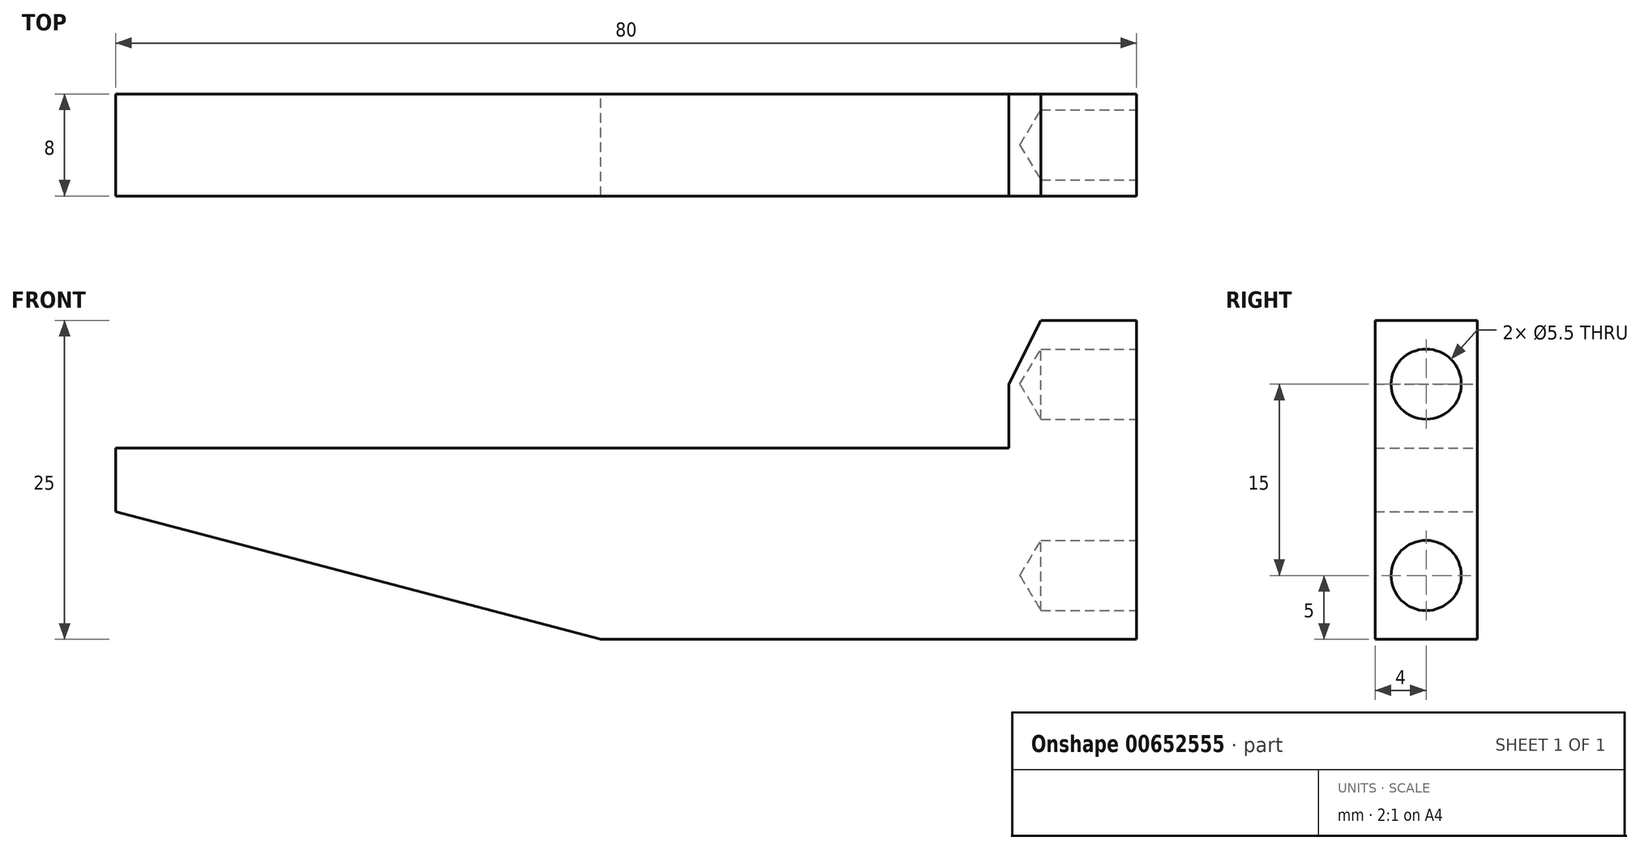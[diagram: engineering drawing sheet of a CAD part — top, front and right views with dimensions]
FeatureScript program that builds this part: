
annotation { "Feature Type Name" : "Feature", "Feature Type Description" : "" }
export const myFeature = defineFeature(function(context is Context, id is Id, definition is map)
    precondition{}
    {
        {
            var Q0;
            Q0=qCreatedBy(makeId("Front.planeOp"),FACE);
            var sketch = newSketch(context, id + "F0", { "sketchPlane" : qUnion([Q0])});
            skLineSegment(sketch, "E0", {"start": v(0, 0) * mm, "end": v(42, 0) * mm});
            skLineSegment(sketch, "E1", {"start": v(42, 0) * mm, "end": v(42, 25) * mm});
            skLineSegment(sketch, "E2", {"start": v(42, 25) * mm, "end": v(34.5, 25) * mm});
            skLineSegment(sketch, "E3", {"start": v(34.5, 25) * mm, "end": v(32, 20) * mm});
            skLineSegment(sketch, "E4", {"start": v(32, 20) * mm, "end": v(32, 15) * mm});
            skLineSegment(sketch, "E5", {"start": v(32, 15) * mm, "end": v(-38, 15) * mm});
            skLineSegment(sketch, "E6", {"start": v(-38, 15) * mm, "end": v(-38, 10) * mm});
            skLineSegment(sketch, "E7", {"start": v(-38, 10) * mm, "end": v(0, 0) * mm});
            skSolve(sketch);
        }
        {
            var Q0;
            Q0=makeQuery(id+"F0.imprint","IMPRINT",FACE,{"disambiguationData":[TD([[makeQuery(id+"F0.imprint","IMPRINT",EDGE,{"derivedFrom":sQuery(id+"F0.wireOp",EDGE,"E0")}),1.0]])]});
            extrude(context, id + "F1", {"entities" : qUnion([Q0]), "depth" : 4 * mm, "offsetDistance" : 25 * mm, "hasSecondDirection" : true, "secondDirectionOppositeDirection" : true, "secondDirectionDepth" : 4 * mm});
        }
        {
            var Q0;
            Q0=makeQuery(id+"F1.opExtrude","SWEPT_FACE",FACE,{"disambiguationData":[OSD([sQuery(id+"F0.wireOp",EDGE,"E1")])]});
            var sketch = newSketch(context, id + "F2", { "sketchPlane" : qUnion([Q0])});
            skPoint(sketch, "E8", {"position": v(0, 20) * mm});
            skPoint(sketch, "E9", {"position": v(0, 5) * mm});
            skSolve(sketch);
        }
        {
            var Q0;
            Q0=sQuery(id+"F2.wireOp",VERTEX,"E8");
            var Q1;
            Q1=sQuery(id+"F2.wireOp",VERTEX,"E9");
            var Q2;
            Q2=makeQuery(id+"F1.opExtrude","SWEPT_BODY",BODY,{"disambiguationData":[OSD([sQuery(id+"F0.wireOp",EDGE,"E0"),sQuery(id+"F0.wireOp",EDGE,"E1"),sQuery(id+"F0.wireOp",EDGE,"E2"),sQuery(id+"F0.wireOp",EDGE,"E3"),sQuery(id+"F0.wireOp",EDGE,"E4"),sQuery(id+"F0.wireOp",EDGE,"E5"),sQuery(id+"F0.wireOp",EDGE,"E6"),sQuery(id+"F0.wireOp",EDGE,"E7")])]});
            hole(context, id + "F3", {"style" : HoleStyle.SIMPLE, "endStyle" : HoleEndStyle.BLIND, "standardTappedOrClearance" : lookupTablePath({ "standard" : "ISO", "fit" : "Normal", "size" : "M5", "type" : "Clearance" }), "standardBlindInLast" : lookupTablePath({ "fit" : "Standard", "standard" : "ISO", "size" : "M5", "type" : "Clearance" }), "holeDiameter" : 5.5 * mm, "majorDiameter" : 5 * mm, "holeDepth" : 7.5 * mm, "isTappedThrough" : true, "tappedDepth" : 12 * mm, "tapClearance" : 3, "locations" : qUnion([Q0, Q1]), "scope" : qUnion([Q2])});
        }
    });
